# Revit family: QF_Kelvinator_738344_KCHUCWT72R-220_3-Door_220V_Refrigerated_Work_Top_72Long
name_source: partatom
category: Specialty Equipment
units: mm (PartAtom-declared; Revit-internal decimal feet)

## family parameters
Always vertical = Yes
Cut with Voids When Loaded = No
Part Type = Normal
Room Calculation Point = No
Round Connector Dimension = Use Diameter
Shared = No
Work Plane-Based = No

## types (1)
- QF_Kelvinator_738344_KCHUCWT72R-220_3-Door_220V_Refrigerated_Work_Top_72Long
    Apparent Power = 0 VA
    Conn Conduit = Yes
    Cycle = 50 Hz
    Default Elevation = 0"
    Depth = 29 15/16"
    Description = 3-Door 220V Refrigerated Work Top 72" Long
    Elec Conn Connection Height = 0"
    Elec Conn RI Height = 0"
    FL Amps = 2 A
    Foodservice Equipment Identifier = Yes
    HP = 1/4
    Height = 39 5/8"
    Identify Quantity as Lot = Yes
    Item Number = 738344
    Length = 71 3/4"
    Manufacturer = Kelvinator Commercial
    Max Overcurrent Protection = 0 A
    Min Ckt Ampacity = 0 A
    Model = 738344 (KCHUCWT72R-220)
    Number of Poles = 1
    Phase = 1
    Refrigerant Type = R290
    Volts = 220 V
    Watts = 396 W
    Weight in Pounds = 380.011

## geometry (parser evidence)
native form markers: Sweep x8
no freeform markers — native parametric forms only
